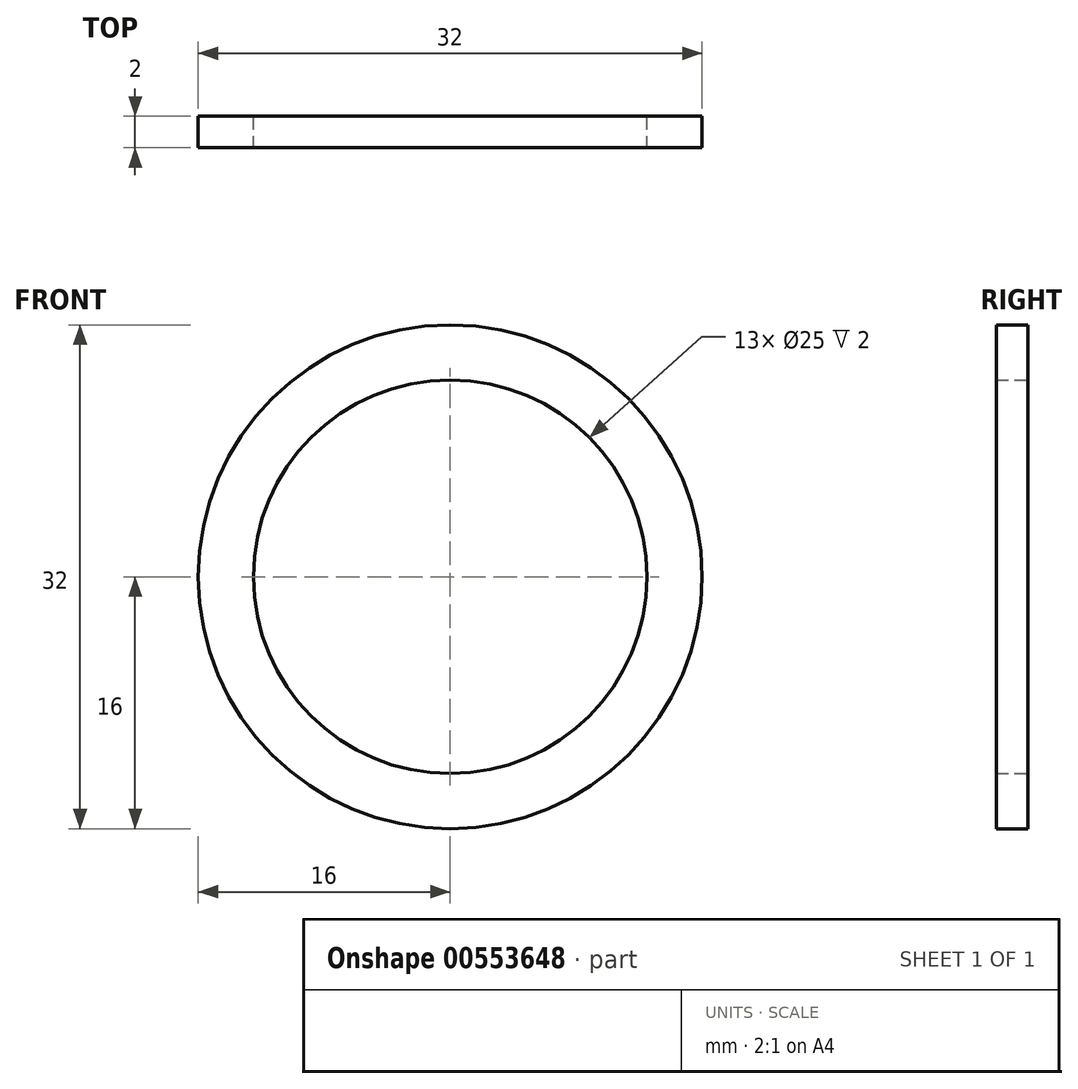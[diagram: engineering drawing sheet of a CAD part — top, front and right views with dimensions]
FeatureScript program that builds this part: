
annotation { "Feature Type Name" : "Feature", "Feature Type Description" : "" }
export const myFeature = defineFeature(function(context is Context, id is Id, definition is map)
    precondition{}
    {
        {
            var Q0;
            Q0=qCreatedBy(makeId("Front.planeOp"),FACE);
            var sketch = newSketch(context, id + "F0", { "sketchPlane" : qUnion([Q0])});
            skCircle(sketch, "E0", {"center": v(0, 0) * mm, "radius": 16 * mm});
            skCircle(sketch, "E1", {"center": v(0, 0) * mm, "radius": 12.5 * mm});
            skSolve(sketch);
        }
        {
            var Q0;
            Q0 = qSketchRegion(id + "F0", true);
            extrude(context, id + "F1", {"entities" : qUnion([Q0]), "depth" : 2 * mm, "offsetDistance" : 25 * mm});
        }
    });
